# Revit family: E-3008-DX
name_source: partatom
category: Plumbing Fixtures
revit_build: Autodesk Revit 2016 (Build: 20150714_1515(x64)
units: mm (PartAtom-declared; Revit-internal decimal feet)

## family parameters
Always vertical = Yes
Cut with Voids When Loaded = No
OmniClass Number = 23.45.00.00
OmniClass Title = Sanitary, Laundry, and Cleaning Equipment
Part Type = Normal
Room Calculation Point = No
Round Connector Dimension = Use Diameter
Shared = Yes
Work Plane-Based = Yes

## types (1)
- E-3008-DX
    Accessories = Contra de push, herramienta para sujeción, placa para empotrar en Tablaroca
    Connection = Conexión ½ -14 NPT
    Default Elevation = 0.0"
    Description = Monomando de pared E-3008-DX
    Gasto Maximo = 1.3 GPM
    Manufacturer = Helvex S.A. de C.V.
    Materials = Cuerpo de latón
    Model = E-3008-DX
    Presión Máxima de Trabajo = 85.3 psi
    Presión Mínima de Trabajo = 14.2 psi
    Product Features = Monomando de Pared Acueducto con Desagüe de Push
    Type Comments = Monomando de Pared E-3008-DX
    URL = http://www.helvex.com.mx

## geometry (parser evidence)
native form markers: Sweep x3
no freeform markers — native parametric forms only
